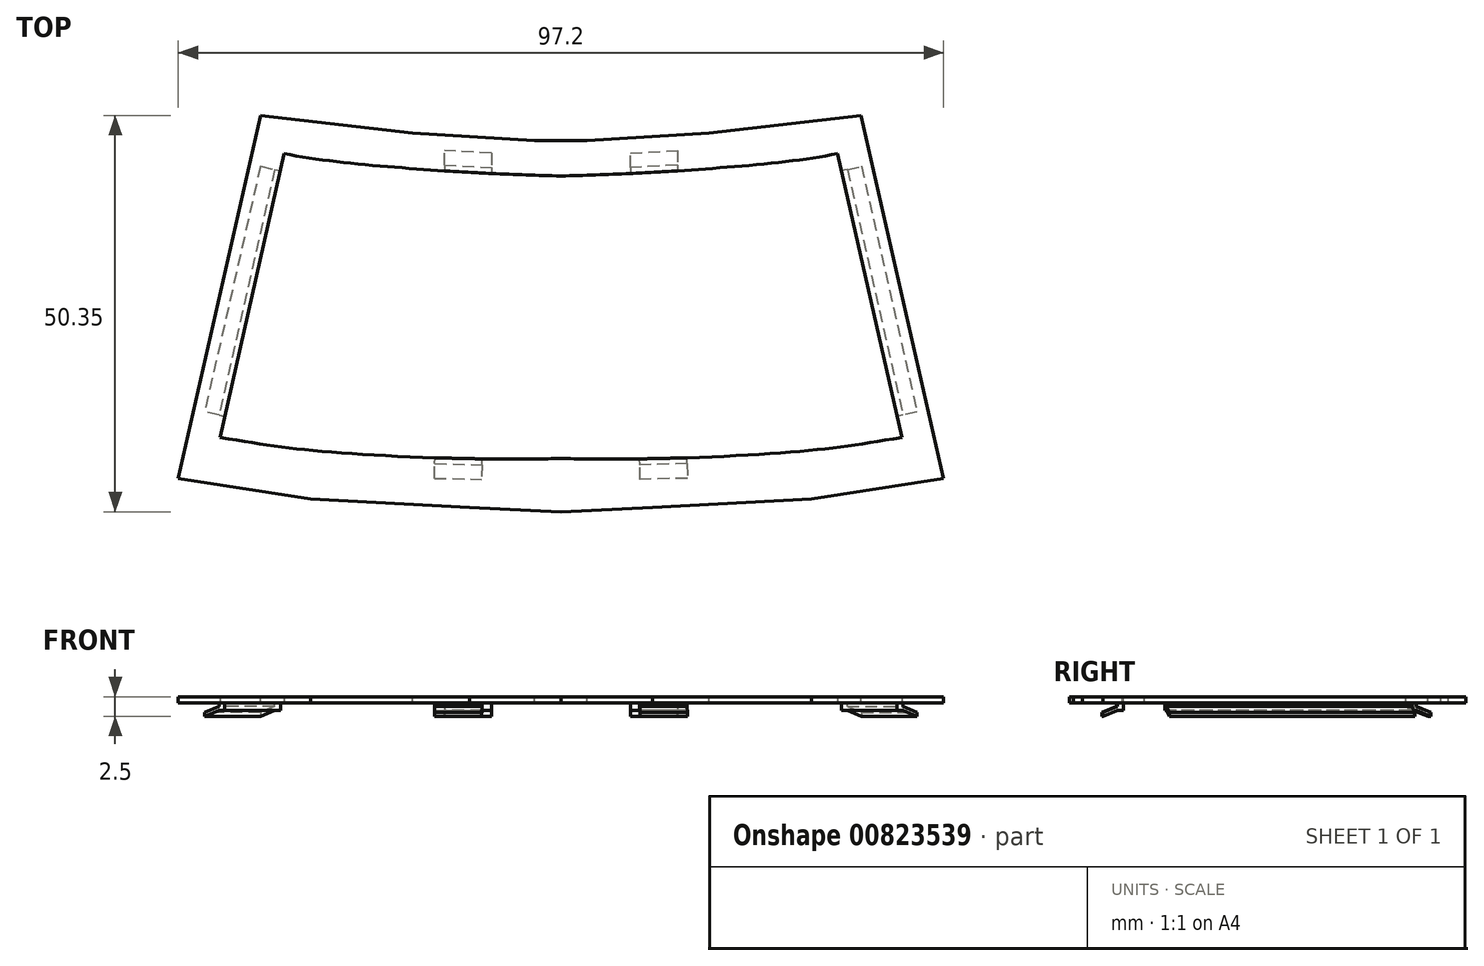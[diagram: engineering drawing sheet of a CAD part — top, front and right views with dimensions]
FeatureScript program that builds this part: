
annotation { "Feature Type Name" : "Feature", "Feature Type Description" : "" }
export const myFeature = defineFeature(function(context is Context, id is Id, definition is map)
    precondition{}
    {
        {
            var Q0;
            Q0=qCreatedBy(makeId("Top.planeOp"),FACE);
            var sketch = newSketch(context, id + "F0", { "sketchPlane" : qUnion([Q0])});
            skLineSegment(sketch, "E0", {"start": v(-37.5, 18.73) * mm, "end": v(0, 18.73) * mm});
            skLineSegment(sketch, "E1", {"start": v(0, -23.15) * mm, "end": v(-47, -23.15) * mm});
            skLineSegment(sketch, "E2", {"start": v(-37.5, 18.73) * mm, "end": v(-47, -23.15) * mm});
            skLineSegment(sketch, "E3", {"start": v(0, 18.73) * mm, "end": v(0, -23.15) * mm});
            skLineSegment(sketch, "E4", {"start": v(0, 18.73) * mm, "end": v(0, 15.73) * mm});
            skLineSegment(sketch, "E5", {"start": v(0, -23.15) * mm, "end": v(0, -26.15) * mm});
            skFitSpline(sketch, "E6", {"points": [v(-37.5, 18.73) * mm, v(-19.53, 16.77) * mm, v(0, 15.73) * mm], "startDerivative": vector(31.33, -4.93) * mm, "endDerivative": vector(43.26, -1.2) * mm});
            skFitSpline(sketch, "E7", {"points": [v(-47, -23.15) * mm, v(-27.96, -25.33) * mm, v(0, -26.15) * mm], "startDerivative": vector(49.87, -5.96) * mm, "endDerivative": vector(44.04, 0.05) * mm});
            skLineSegment(sketch, "E8", {"start": v(0, 15.73) * mm, "end": v(0, 12.73) * mm});
            skLineSegment(sketch, "E9", {"start": v(-35.14, 15.56) * mm, "end": v(-43.32, -20.47) * mm});
            skFitSpline(sketch, "E10", {"points": [v(-35.14, 15.56) * mm, v(-18.26, 13.62) * mm, v(0, 12.73) * mm], "startDerivative": vector(28.47, -5.7) * mm, "endDerivative": vector(41.53, -1.04) * mm});
            skFitSpline(sketch, "E11", {"points": [v(-43.32, -20.47) * mm, v(-30.15, -22.27) * mm, v(0, -23.15) * mm], "startDerivative": vector(37.03, -6.22) * mm, "endDerivative": vector(49.4, 1.38) * mm});
            skLineSegment(sketch, "E12", {"start": v(-36.37, 13.56) * mm, "end": v(-43.44, -17.65) * mm});
            skLineSegment(sketch, "E13", {"start": v(-36.37, 13.56) * mm, "end": v(-35.64, 13.4) * mm});
            skLineSegment(sketch, "E14", {"start": v(-43.44, -17.65) * mm, "end": v(-42.71, -17.82) * mm});
            skLineSegment(sketch, "E15", {"start": v(-14.8, 14.13) * mm, "end": v(-8.81, 13.8) * mm});
            skLineSegment(sketch, "E16", {"start": v(-14.8, 14.13) * mm, "end": v(-14.8, 13.38) * mm});
            skLineSegment(sketch, "E17", {"start": v(-8.81, 13.8) * mm, "end": v(-8.81, 13.04) * mm});
            skLineSegment(sketch, "E18", {"start": v(-16.02, -23.81) * mm, "end": v(-10.03, -23.96) * mm});
            skLineSegment(sketch, "E19", {"start": v(-10.03, -23.96) * mm, "end": v(-10, -23.2) * mm});
            skLineSegment(sketch, "E20", {"start": v(-16.02, -23.81) * mm, "end": v(-16, -23.06) * mm});
            skSolve(sketch);
        }
        {
            var Q0;
            {var subQ12=sQuery(id+"F0.wireOp",EDGE,"E2");Q0=makeQuery(id+"F0.imprint","IMPRINT",FACE,{"disambiguationData":[TD([[makeQuery(id+"F0.imprint","IMPRINT",EDGE,{"derivedFrom":subQ12}),1.0]])]});}
            var Q1;
            Q1=makeQuery(id+"F0.imprint","IMPRINT",FACE,{"disambiguationData":[TD([[makeQuery(id+"F0.imprint","IMPRINT",EDGE,{"derivedFrom":sQuery(id+"F0.wireOp",EDGE,"E12")}),1.0]])]});
            var Q2;
            {var subQ1=sQuery(id+"F0.wireOp",EDGE,"E5");Q2=makeQuery(id+"F0.imprint","IMPRINT",FACE,{"disambiguationData":[TD([[makeQuery(id+"F0.imprint","IMPRINT",EDGE,{"derivedFrom":subQ1}),-1.0]])]});}
            var Q3;
            {var subQ4=sQuery(id+"F0.wireOp",EDGE,"E18");Q3=makeQuery(id+"F0.imprint","IMPRINT",FACE,{"disambiguationData":[TD([[makeQuery(id+"F0.imprint","IMPRINT",EDGE,{"derivedFrom":subQ4}),1.0]])]});}
            var Q4;
            {var subQ0=sQuery(id+"F0.wireOp",EDGE,"E11");var subQ1=sQuery(id+"F0.wireOp",EDGE,"E1");var subQ2=makeQuery(id+"F0.imprint","INTERSECT",VERTEX,{"derivedFrom":[subQ1,subQ0]});Q4=makeQuery(id+"F0.imprint","IMPRINT",FACE,{"disambiguationData":[TD([[makeQuery(id+"F0.imprint","IMPRINT",EDGE,{"disambiguationData":[TD([[subQ2,-1.0]])],"derivedFrom":subQ1}),-1.0]])]});}
            var Q5;
            Q5=makeQuery(id+"F0.imprint","IMPRINT",FACE,{"disambiguationData":[TD([[makeQuery(id+"F0.imprint","IMPRINT",EDGE,{"derivedFrom":sQuery(id+"F0.wireOp",EDGE,"E15")}),-1.0]])]});
            extrude(context, id + "F1", {"entities" : qUnion([Q0, Q1, Q2, Q3, Q4, Q5]), "depth" : .75 * mm, "offsetDistance" : 25 * mm});
        }
        {
            var Q0;
            Q0=makeQuery(id+"F0.imprint","IMPRINT",FACE,{"disambiguationData":[TD([[makeQuery(id+"F0.imprint","IMPRINT",EDGE,{"derivedFrom":sQuery(id+"F0.wireOp",EDGE,"E15")}),-1.0]])]});
            var Q1;
            Q1=makeQuery(id+"F0.imprint","IMPRINT",FACE,{"disambiguationData":[TD([[makeQuery(id+"F0.imprint","IMPRINT",EDGE,{"derivedFrom":sQuery(id+"F0.wireOp",EDGE,"E12")}),1.0]])]});
            var Q2;
            {var subQ4=sQuery(id+"F0.wireOp",EDGE,"E18");Q2=makeQuery(id+"F0.imprint","IMPRINT",FACE,{"disambiguationData":[TD([[makeQuery(id+"F0.imprint","IMPRINT",EDGE,{"derivedFrom":subQ4}),1.0]])]});}
            var Q3;
            {var subQ0=sQuery(id+"F0.wireOp",EDGE,"E11");var subQ1=sQuery(id+"F0.wireOp",EDGE,"E1");var subQ2=makeQuery(id+"F0.imprint","INTERSECT",VERTEX,{"derivedFrom":[subQ1,subQ0]});Q3=makeQuery(id+"F0.imprint","IMPRINT",FACE,{"disambiguationData":[TD([[makeQuery(id+"F0.imprint","IMPRINT",EDGE,{"disambiguationData":[TD([[subQ2,-1.0]])],"derivedFrom":subQ1}),-1.0]])]});}
            extrude(context, id + "F2", {"entities" : qUnion([Q0, Q1, Q2, Q3]), "operationType" : NewBodyOperationType.ADD, "oppositeDirection" : true, "depth" : 1 * mm, "offsetDistance" : 25 * mm});
        }
        {
            var Q0;
            Q0=makeQuery(id+"F1.opExtrude","CAP_FACE",FACE,{"disambiguationData":[OSD([sQuery(id+"F0.wireOp",EDGE,"E2"),sQuery(id+"F0.wireOp",EDGE,"E5"),sQuery(id+"F0.wireOp",EDGE,"E6"),sQuery(id+"F0.wireOp",EDGE,"E7"),sQuery(id+"F0.wireOp",EDGE,"E8"),sQuery(id+"F0.wireOp",EDGE,"E9"),sQuery(id+"F0.wireOp",EDGE,"E10"),sQuery(id+"F0.wireOp",EDGE,"E11")])],"isStart":false});
            var sketch = newSketch(context, id + "F3", { "sketchPlane" : qUnion([Q0])});
            skLineSegment(sketch, "E21", {"start": v(-47, -23.15) * mm, "end": v(-37.5, 18.73) * mm});
            skLineSegment(sketch, "E22", {"start": v(-37.5, 18.73) * mm, "end": v(-38.48, 18.95) * mm});
            skLineSegment(sketch, "E23", {"start": v(-38.48, 18.95) * mm, "end": v(-47.98, -22.93) * mm});
            skLineSegment(sketch, "E24", {"start": v(-47.98, -22.93) * mm, "end": v(-47, -23.15) * mm});
            skSolve(sketch);
        }
        {
            var Q0;
            Q0=makeQuery(id+"F3.imprint","IMPRINT",FACE,{"disambiguationData":[TD([[makeQuery(id+"F3.imprint","IMPRINT",EDGE,{"derivedFrom":sQuery(id+"F3.wireOp",EDGE,"E21")}),-1.0]])]});
            var Q1;
            Q1=makeQuery(id+"F1.opExtrude","CAP_FACE",FACE,{"disambiguationData":[OSD([sQuery(id+"F0.wireOp",EDGE,"E2"),sQuery(id+"F0.wireOp",EDGE,"E5"),sQuery(id+"F0.wireOp",EDGE,"E6"),sQuery(id+"F0.wireOp",EDGE,"E7"),sQuery(id+"F0.wireOp",EDGE,"E8"),sQuery(id+"F0.wireOp",EDGE,"E9"),sQuery(id+"F0.wireOp",EDGE,"E10"),sQuery(id+"F0.wireOp",EDGE,"E11")])],"isStart":true});
            extrude(context, id + "F4", {"entities" : qUnion([Q0]), "operationType" : NewBodyOperationType.ADD, "endBound" : BoundingType.UP_TO_SURFACE, "oppositeDirection" : true, "depth" : 25 * mm, "endBoundEntityFace" : qUnion([Q1]), "offsetDistance" : 25 * mm});
        }
        {
            var Q0;
            Q0=makeQuery(id+"F4.boolean.opBoolean","MERGE",FACE,{"derivedFrom":[makeQuery(id+"F1.opExtrude","CAP_FACE",FACE,{"disambiguationData":[OSD([sQuery(id+"F0.wireOp",EDGE,"E2"),sQuery(id+"F0.wireOp",EDGE,"E5"),sQuery(id+"F0.wireOp",EDGE,"E6"),sQuery(id+"F0.wireOp",EDGE,"E7"),sQuery(id+"F0.wireOp",EDGE,"E8"),sQuery(id+"F0.wireOp",EDGE,"E9"),sQuery(id+"F0.wireOp",EDGE,"E10"),sQuery(id+"F0.wireOp",EDGE,"E11")])],"isStart":false}),makeQuery(id+"F4.opExtrude","CAP_FACE",FACE,{"disambiguationData":[OSD([sQuery(id+"F3.wireOp",EDGE,"E21"),sQuery(id+"F3.wireOp",EDGE,"E22"),sQuery(id+"F3.wireOp",EDGE,"E23"),sQuery(id+"F3.wireOp",EDGE,"E24")])],"isStart":true})]});
            var sketch = newSketch(context, id + "F5", { "sketchPlane" : qUnion([Q0])});
            skLineSegment(sketch, "E25", {"start": v(-38.48, 18.95) * mm, "end": v(-38.14, 20.42) * mm});
            skLineSegment(sketch, "E26", {"start": v(-38.14, 20.42) * mm, "end": v(-18.83, 18.21) * mm});
            skLineSegment(sketch, "E27", {"start": v(-18.83, 18.21) * mm, "end": v(-3.32, 17.23) * mm});
            skLineSegment(sketch, "E28", {"start": v(-3.32, 17.23) * mm, "end": v(0, 17.23) * mm});
            skLineSegment(sketch, "E29", {"start": v(0, 17.23) * mm, "end": v(0, 15.73) * mm});
            skSolve(sketch);
        }
        {
            var Q0;
            Q0=makeQuery(id+"F5.imprint","IMPRINT",FACE,{"disambiguationData":[TD([[makeQuery(id+"F5.imprint","IMPRINT",EDGE,{"derivedFrom":sQuery(id+"F5.wireOp",EDGE,"E25")}),-1.0]])]});
            var Q1;
            {var subQ0=sQuery(id+"F0.wireOp",EDGE,"E11");var subQ1=sQuery(id+"F0.wireOp",EDGE,"E10");var subQ2=sQuery(id+"F0.wireOp",EDGE,"E9");var subQ3=sQuery(id+"F0.wireOp",EDGE,"E8");var subQ4=sQuery(id+"F0.wireOp",EDGE,"E7");var subQ5=sQuery(id+"F0.wireOp",EDGE,"E6");var subQ6=sQuery(id+"F0.wireOp",EDGE,"E5");var subQ7=sQuery(id+"F0.wireOp",EDGE,"E2");Q1=makeQuery(id+"F4.boolean.opBoolean","MERGE",FACE,{"derivedFrom":[makeQuery(id+"F1.opExtrude","CAP_FACE",FACE,{"disambiguationData":[OSD([subQ7,subQ6,subQ5,subQ4,subQ3,subQ2,subQ1,subQ0])],"isStart":true}),makeQuery(id+"F4.opExtrude","CAP_FACE",FACE,{"disambiguationData":[OSD([subQ7,subQ6,subQ5,subQ4,subQ3,subQ2,subQ1,subQ0])],"isStart":false})]});}
            extrude(context, id + "F6", {"entities" : qUnion([Q0]), "operationType" : NewBodyOperationType.ADD, "endBound" : BoundingType.UP_TO_SURFACE, "oppositeDirection" : true, "depth" : 25 * mm, "endBoundEntityFace" : qUnion([Q1]), "offsetDistance" : 25 * mm});
        }
        {
            var Q0;
            {var subQ0=sQuery(id+"F3.wireOp",EDGE,"E22");var subQ1=sQuery(id+"F0.wireOp",EDGE,"E6");Q0=makeQuery(id+"F6.boolean.opBoolean","MERGE",FACE,{"derivedFrom":[makeQuery(id+"F4.boolean.opBoolean","MERGE",FACE,{"derivedFrom":[makeQuery(id+"F1.opExtrude","CAP_FACE",FACE,{"disambiguationData":[OSD([sQuery(id+"F0.wireOp",EDGE,"E2"),sQuery(id+"F0.wireOp",EDGE,"E5"),subQ1,sQuery(id+"F0.wireOp",EDGE,"E7"),sQuery(id+"F0.wireOp",EDGE,"E8"),sQuery(id+"F0.wireOp",EDGE,"E9"),sQuery(id+"F0.wireOp",EDGE,"E10"),sQuery(id+"F0.wireOp",EDGE,"E11")])],"isStart":false}),makeQuery(id+"F4.opExtrude","CAP_FACE",FACE,{"disambiguationData":[OSD([sQuery(id+"F3.wireOp",EDGE,"E21"),subQ0,sQuery(id+"F3.wireOp",EDGE,"E23"),sQuery(id+"F3.wireOp",EDGE,"E24")])],"isStart":true})]}),makeQuery(id+"F6.opExtrude","CAP_FACE",FACE,{"disambiguationData":[OSD([subQ1,subQ0,sQuery(id+"F5.wireOp",EDGE,"E25"),sQuery(id+"F5.wireOp",EDGE,"E26"),sQuery(id+"F5.wireOp",EDGE,"E27"),sQuery(id+"F5.wireOp",EDGE,"E28"),sQuery(id+"F5.wireOp",EDGE,"E29")])],"isStart":true})]});}
            var sketch = newSketch(context, id + "F7", { "sketchPlane" : qUnion([Q0])});
            skLineSegment(sketch, "E30", {"start": v(-47.98, -22.93) * mm, "end": v(-48.6, -25.69) * mm});
            skLineSegment(sketch, "E31", {"start": v(-48.6, -25.69) * mm, "end": v(-31.8, -28.29) * mm});
            skLineSegment(sketch, "E32", {"start": v(-31.8, -28.29) * mm, "end": v(-11.6, -29.41) * mm});
            skLineSegment(sketch, "E33", {"start": v(-11.6, -29.41) * mm, "end": v(0, -29.93) * mm});
            skLineSegment(sketch, "E34", {"start": v(0, -29.93) * mm, "end": v(0, -26.15) * mm});
            skSolve(sketch);
        }
        {
            var Q0;
            Q0=makeQuery(id+"F7.imprint","IMPRINT",FACE,{"disambiguationData":[TD([[makeQuery(id+"F7.imprint","IMPRINT",EDGE,{"derivedFrom":sQuery(id+"F7.wireOp",EDGE,"E30")}),1.0]])]});
            var Q1;
            {var subQ0=sQuery(id+"F0.wireOp",EDGE,"E11");var subQ1=sQuery(id+"F0.wireOp",EDGE,"E10");var subQ2=sQuery(id+"F0.wireOp",EDGE,"E9");var subQ3=sQuery(id+"F0.wireOp",EDGE,"E8");var subQ4=sQuery(id+"F0.wireOp",EDGE,"E7");var subQ5=sQuery(id+"F0.wireOp",EDGE,"E6");var subQ6=sQuery(id+"F0.wireOp",EDGE,"E5");var subQ7=sQuery(id+"F0.wireOp",EDGE,"E2");Q1=makeQuery(id+"F6.boolean.opBoolean","MERGE",FACE,{"derivedFrom":[makeQuery(id+"F4.boolean.opBoolean","MERGE",FACE,{"derivedFrom":[makeQuery(id+"F1.opExtrude","CAP_FACE",FACE,{"disambiguationData":[OSD([subQ7,subQ6,subQ5,subQ4,subQ3,subQ2,subQ1,subQ0])],"isStart":true}),makeQuery(id+"F4.opExtrude","CAP_FACE",FACE,{"disambiguationData":[OSD([subQ7,subQ6,subQ5,subQ4,subQ3,subQ2,subQ1,subQ0])],"isStart":false})]}),makeQuery(id+"F6.opExtrude","CAP_FACE",FACE,{"disambiguationData":[OSD([subQ7,subQ6,subQ5,subQ4,subQ3,subQ2,subQ1,subQ0])],"isStart":false})]});}
            extrude(context, id + "F8", {"entities" : qUnion([Q0]), "operationType" : NewBodyOperationType.ADD, "endBound" : BoundingType.UP_TO_SURFACE, "oppositeDirection" : true, "depth" : 25 * mm, "endBoundEntityFace" : qUnion([Q1]), "offsetDistance" : 25 * mm});
        }
        {
            var Q0;
            Q0=makeQuery(id+"F2.opExtrude","SWEPT_FACE",FACE,{"disambiguationData":[OSD([sQuery(id+"F0.wireOp",EDGE,"E17")])]});
            var sketch = newSketch(context, id + "F9", { "sketchPlane" : qUnion([Q0])});
            skLineSegment(sketch, "E35", {"start": v(13.8, -1) * mm, "end": v(13.8, -0.5) * mm});
            skLineSegment(sketch, "E36", {"start": v(13.8, -0.5) * mm, "end": v(15.65, -1.25) * mm});
            skLineSegment(sketch, "E37", {"start": v(15.65, -1.25) * mm, "end": v(15.65, -1.75) * mm});
            skLineSegment(sketch, "E38", {"start": v(15.65, -1.75) * mm, "end": v(13.8, -1) * mm});
            skSolve(sketch);
        }
        {
            var Q0;
            Q0=makeQuery(id+"F2.opExtrude","SWEPT_FACE",FACE,{"disambiguationData":[OSD([sQuery(id+"F0.wireOp",EDGE,"E16")])]});
            var sketch = newSketch(context, id + "F10", { "sketchPlane" : qUnion([Q0])});
            skLineSegment(sketch, "E39", {"start": v(-14.13, -1) * mm, "end": v(-14.13, -0.5) * mm});
            skLineSegment(sketch, "E40", {"start": v(-14.13, -0.5) * mm, "end": v(-15.99, -1.25) * mm});
            skLineSegment(sketch, "E41", {"start": v(-15.99, -1.25) * mm, "end": v(-15.99, -1.75) * mm});
            skLineSegment(sketch, "E42", {"start": v(-15.99, -1.75) * mm, "end": v(-14.13, -1) * mm});
            skSolve(sketch);
        }
        {
            var Q1;
            Q1=makeQuery(id+"F9.imprint","IMPRINT",FACE,{"disambiguationData":[TD([[makeQuery(id+"F9.imprint","IMPRINT",EDGE,{"derivedFrom":sQuery(id+"F9.wireOp",EDGE,"E35")}),-1.0]])]});
            var Q2;
            Q2=makeQuery(id+"F10.imprint","IMPRINT",FACE,{"disambiguationData":[TD([[makeQuery(id+"F10.imprint","IMPRINT",EDGE,{"derivedFrom":sQuery(id+"F10.wireOp",EDGE,"E39")}),1.0]])]});
            loft(context, id + "F11", {"operationType" : NewBodyOperationType.ADD, "sheetProfilesArray" : [{ "sheetProfileEntities" : qUnion([Q1]) }, { "sheetProfileEntities" : qUnion([Q2]) }]});
        }
        {
            var Q0;
            Q0=makeQuery(id+"F2.opExtrude","SWEPT_FACE",FACE,{"disambiguationData":[OSD([sQuery(id+"F0.wireOp",EDGE,"E20")])]});
            var sketch = newSketch(context, id + "F12", { "sketchPlane" : qUnion([Q0])});
            skLineSegment(sketch, "E43", {"start": v(24.18, -1) * mm, "end": v(24.18, -0.5) * mm});
            skLineSegment(sketch, "E44", {"start": v(24.18, -0.5) * mm, "end": v(26.04, -1.25) * mm});
            skLineSegment(sketch, "E45", {"start": v(26.04, -1.25) * mm, "end": v(26.04, -1.75) * mm});
            skLineSegment(sketch, "E46", {"start": v(26.04, -1.75) * mm, "end": v(24.18, -1) * mm});
            skSolve(sketch);
        }
        {
            var Q0;
            Q0=makeQuery(id+"F2.opExtrude","SWEPT_FACE",FACE,{"disambiguationData":[OSD([sQuery(id+"F0.wireOp",EDGE,"E19")])]});
            var sketch = newSketch(context, id + "F13", { "sketchPlane" : qUnion([Q0])});
            skLineSegment(sketch, "E47", {"start": v(-24.18, -1) * mm, "end": v(-24.18, -0.5) * mm});
            skLineSegment(sketch, "E48", {"start": v(-24.18, -0.5) * mm, "end": v(-26.04, -1.25) * mm});
            skLineSegment(sketch, "E49", {"start": v(-26.04, -1.25) * mm, "end": v(-26.04, -1.75) * mm});
            skLineSegment(sketch, "E50", {"start": v(-26.04, -1.75) * mm, "end": v(-24.18, -1) * mm});
            skSolve(sketch);
        }
        {
            var Q1;
            Q1=makeQuery(id+"F12.imprint","IMPRINT",FACE,{"disambiguationData":[TD([[makeQuery(id+"F12.imprint","IMPRINT",EDGE,{"derivedFrom":sQuery(id+"F12.wireOp",EDGE,"E43")}),-1.0]])]});
            var Q2;
            Q2=makeQuery(id+"F13.imprint","IMPRINT",FACE,{"disambiguationData":[TD([[makeQuery(id+"F13.imprint","IMPRINT",EDGE,{"derivedFrom":sQuery(id+"F13.wireOp",EDGE,"E47")}),1.0]])]});
            loft(context, id + "F14", {"operationType" : NewBodyOperationType.ADD, "sheetProfilesArray" : [{ "sheetProfileEntities" : qUnion([Q1]) }, { "sheetProfileEntities" : qUnion([Q2]) }]});
        }
        {
            var Q0;
            Q0=makeQuery(id+"F2.opExtrude","SWEPT_FACE",FACE,{"disambiguationData":[OSD([sQuery(id+"F0.wireOp",EDGE,"E13")])]});
            var sketch = newSketch(context, id + "F15", { "sketchPlane" : qUnion([Q0])});
            skLineSegment(sketch, "E51", {"start": v(38.46, -1) * mm, "end": v(38.46, -0.5) * mm});
            skLineSegment(sketch, "E52", {"start": v(38.46, -0.5) * mm, "end": v(40.32, -1.25) * mm});
            skLineSegment(sketch, "E53", {"start": v(40.32, -1.25) * mm, "end": v(40.32, -1.75) * mm});
            skLineSegment(sketch, "E54", {"start": v(40.32, -1.75) * mm, "end": v(38.46, -1) * mm});
            skSolve(sketch);
        }
        {
            var Q0;
            Q0=makeQuery(id+"F2.opExtrude","SWEPT_FACE",FACE,{"disambiguationData":[OSD([sQuery(id+"F0.wireOp",EDGE,"E14")])]});
            var sketch = newSketch(context, id + "F16", { "sketchPlane" : qUnion([Q0])});
            skLineSegment(sketch, "E55", {"start": v(-38.46, -1) * mm, "end": v(-38.46, -0.5) * mm});
            skLineSegment(sketch, "E56", {"start": v(-38.46, -0.5) * mm, "end": v(-40.32, -1.25) * mm});
            skLineSegment(sketch, "E57", {"start": v(-40.32, -1.25) * mm, "end": v(-40.32, -1.75) * mm});
            skLineSegment(sketch, "E58", {"start": v(-40.32, -1.75) * mm, "end": v(-38.46, -1) * mm});
            skSolve(sketch);
        }
        {
            var Q1;
            Q1=makeQuery(id+"F15.imprint","IMPRINT",FACE,{"disambiguationData":[TD([[makeQuery(id+"F15.imprint","IMPRINT",EDGE,{"derivedFrom":sQuery(id+"F15.wireOp",EDGE,"E51")}),-1.0]])]});
            var Q2;
            Q2=makeQuery(id+"F16.imprint","IMPRINT",FACE,{"disambiguationData":[TD([[makeQuery(id+"F16.imprint","IMPRINT",EDGE,{"derivedFrom":sQuery(id+"F16.wireOp",EDGE,"E55")}),1.0]])]});
            loft(context, id + "F17", {"operationType" : NewBodyOperationType.ADD, "sheetProfilesArray" : [{ "sheetProfileEntities" : qUnion([Q1]) }, { "sheetProfileEntities" : qUnion([Q2]) }]});
        }
        {
            var Q0;
            Q0=makeQuery(id+"F1.opExtrude","SWEPT_BODY",BODY,{"disambiguationData":[OSD([sQuery(id+"F0.wireOp",EDGE,"E2"),sQuery(id+"F0.wireOp",EDGE,"E5"),sQuery(id+"F0.wireOp",EDGE,"E6"),sQuery(id+"F0.wireOp",EDGE,"E7"),sQuery(id+"F0.wireOp",EDGE,"E8"),sQuery(id+"F0.wireOp",EDGE,"E9"),sQuery(id+"F0.wireOp",EDGE,"E10"),sQuery(id+"F0.wireOp",EDGE,"E11")])]});
            var Q1;
            Q1=qCreatedBy(makeId("Right.planeOp"),FACE);
            mirror(context, id + "F18", {"operationType" : NewBodyOperationType.ADD, "entities" : qUnion([Q0]), "mirrorPlane" : qUnion([Q1])});
        }
    });
